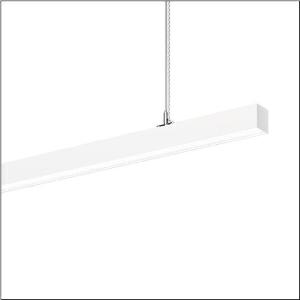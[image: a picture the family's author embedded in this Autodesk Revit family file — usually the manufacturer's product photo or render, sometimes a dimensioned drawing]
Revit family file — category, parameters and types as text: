
# Revit family: silica_r__21_51mx30dc49wb_27b8
name_source: partatom
category: Lighting Fixtures
units: mm (PartAtom-declared; Revit-internal decimal feet)

## family parameters
Cut with Voids When Loaded = No
Host = Face
Light Source = No
Part Type = Normal
Room Calculation Point = No
Round Connector Dimension = Use Diameter
Shared = No

## types (1)
- --- (1 x LED, 10520 lm, 64.1 W, 4000K)
    Apparent Load = 64 VA
    CIE Flux Codes = 47 79 96 57 100
    Color Rendering = 80
    Color Temperature = 4000K
    Default Elevation = 1800 mm
    Description = Silica® 21, office luminaire, primary optical cover: cover, of PMMA, opal, light emission: direct/indirect distribution, primary light characteristic: symmetric, installation type: suspended mounting, LED, rated luminous flux: 10.520lm, luminous efficacy: 164lm/W, light colour: 840, colour temperature: 4000K, with terminal, 3+2-pole, max. 2.5mm², mains connection: 220..240V, AC, 50/60Hz, rated input power: 64.1W, luminaire housing, of aluminium, traffic white (RAL 9016), length: 3.004mm, width: 53mm, height: 53mm, protection rating (complete): IP20, insulation class (complete): insulation class I (protective earthing), certification: CE, permissible operating ambient temperature: 0..+35°C, standard: EN 50419, packaging unit: 1 piece
    Height = 53 mm
    Lamp = 1 x LED
    Lamp Light Flux = 10520 lm
    Lamp Power = 64.1 W
    Lamp count = 1
    Length = 3004 mm
    Luminous efficacy = 164 lm/W
    Manufacturer = Siteco
    ModVariant = No
    Model = 51MX30DC49WB
    Mounting Place = Ceiling
    Mounting Type = Pendant
    Number of Poles = 1
    OnlyDefault = Yes
    Power Factor = 1
    Product Name = Silica® 21
    Product group = office luminaire | ceiling pendant
    ProductGroupID = 902
    Protection Class = Protection class I
    Protection Degree = IP 20
    RLX_Detail_Level = 1
    RLX_Emergency_Light_Flux = 0 lm
    RLX_Emergency_Type = 0
    RLX_Emergency_Type_DB = No
    RlxData = <blob elided: 21313 chars, md5=df08e35f>
    Socket = socket
    Standby Power = 0 W
    System Light Flux = 10520 lm
    System Power = 64 W
    Type Comments = factory setting: luminous flux: 100 % | dim-lin: 254 | 218 mA
    Type Image = l_1313629.jpg
    URL = http://relux.com
    VarID = @adj_065629
    Voltage = 0 V
    Weight = 0.00 kg
    Width = 53 mm

## geometry (parser evidence)
native form markers: Blend x4, Sweep x14
no freeform markers — native parametric forms only
